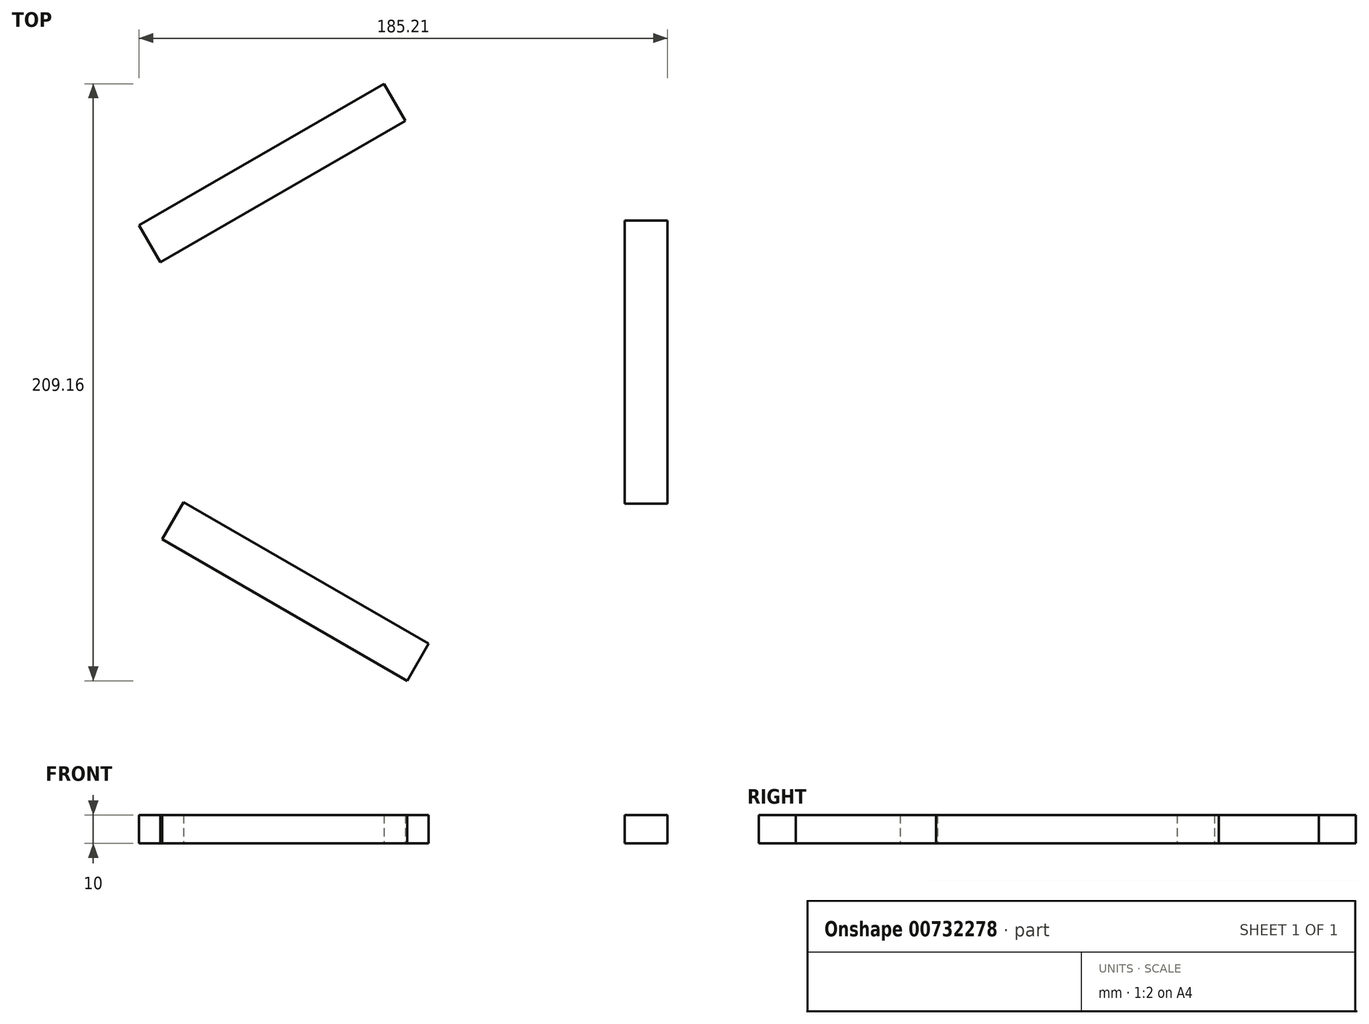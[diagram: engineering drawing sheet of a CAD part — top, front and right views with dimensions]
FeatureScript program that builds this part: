
annotation { "Feature Type Name" : "Feature", "Feature Type Description" : "" }
export const myFeature = defineFeature(function(context is Context, id is Id, definition is map)
    precondition{}
    {
        {
            var Q0;
            Q0=qCreatedBy(makeId("Top.planeOp"),FACE);
            var sketch = newSketch(context, id + "F0", { "sketchPlane" : qUnion([Q0])});
            skLineSegment(sketch, "E0.bottom", {"start": v(-44.37, 77.42) * mm, "end": v(-57.36, 84.92) * mm});
            skLineSegment(sketch, "E0.top", {"start": v(-93.94, -8.43) * mm, "end": v(-106.93, -0.93) * mm});
            skLineSegment(sketch, "E0.left", {"start": v(-44.37, 77.42) * mm, "end": v(-93.94, -8.43) * mm});
            skLineSegment(sketch, "E0.right", {"start": v(-57.36, 84.92) * mm, "end": v(-106.93, -0.93) * mm});
            skPoint(sketch, "E0.middle", {"position": v(-78.55, -220.5) * mm});
            skCircle(sketch, "E1", {"center": v(0, 0) * mm, "radius": 77.14 * mm, "construction": true});
            skLineSegment(sketch, "E2", {"start": v(-75.65, 38.25) * mm, "end": v(-53.37, 76.84) * mm});
            skLineSegment(sketch, "E3", {"start": v(-75.65, 38.25) * mm, "end": v(-97.94, -0.35) * mm});
            skLineSegment(sketch, "E4.bottom", {"start": v(51.27, 95.48) * mm, "end": v(38.28, 87.98) * mm});
            skLineSegment(sketch, "E4.top", {"start": v(100.84, 9.62) * mm, "end": v(87.85, 2.12) * mm});
            skLineSegment(sketch, "E4.left", {"start": v(51.27, 95.48) * mm, "end": v(100.84, 9.62) * mm});
            skLineSegment(sketch, "E4.right", {"start": v(38.28, 87.98) * mm, "end": v(87.85, 2.12) * mm});
            skPoint(sketch, "E4.middle", {"position": v(69.56, 48.8) * mm});
            skLineSegment(sketch, "E5", {"start": v(69.56, 48.8) * mm, "end": v(47.28, 87.4) * mm});
            skLineSegment(sketch, "E6", {"start": v(69.56, 48.8) * mm, "end": v(91.85, 10.2) * mm});
            skLineSegment(sketch, "E7.bottom", {"start": v(-48.28, -78.45) * mm, "end": v(-48.28, -93.45) * mm});
            skLineSegment(sketch, "E7.top", {"start": v(50.86, -78.45) * mm, "end": v(50.86, -93.45) * mm});
            skLineSegment(sketch, "E7.left", {"start": v(-48.28, -78.45) * mm, "end": v(50.86, -78.45) * mm});
            skLineSegment(sketch, "E7.right", {"start": v(-48.28, -93.45) * mm, "end": v(50.86, -93.45) * mm});
            skPoint(sketch, "E7.middle", {"position": v(1.3, -85.95) * mm});
            skLineSegment(sketch, "E8", {"start": v(1.3, -85.95) * mm, "end": v(-43.28, -85.95) * mm});
            skLineSegment(sketch, "E9", {"start": v(1.3, -85.95) * mm, "end": v(45.86, -85.95) * mm});
            skLineSegment(sketch, "E10.bottom", {"start": v(-9.28, 107.28) * mm, "end": v(-22.27, 114.78) * mm});
            skLineSegment(sketch, "E10.top", {"start": v(-108.84, -65.17) * mm, "end": v(-121.83, -57.67) * mm});
            skLineSegment(sketch, "E10.left", {"start": v(-9.28, 107.28) * mm, "end": v(-108.84, -65.17) * mm});
            skLineSegment(sketch, "E10.right", {"start": v(-22.27, 114.78) * mm, "end": v(-121.83, -57.67) * mm});
            skSolve(sketch);
        }
        {
            var Q0;
            Q0=makeQuery(id+"F0.imprint","IMPRINT",FACE,{"disambiguationData":[TD([[makeQuery(id+"F0.imprint","IMPRINT",EDGE,{"derivedFrom":sQuery(id+"F0.wireOp",EDGE,"E0.bottom")}),1.0]])]});
            extrude(context, id + "F1", {"entities" : qUnion([Q0]), "depth" : 10 * mm, "offsetDistance" : 25 * mm});
        }
        {
            var Q0;
            Q0=makeQuery(id+"F1.opExtrude","SWEPT_BODY",BODY,{"disambiguationData":[OSD([sQuery(id+"F0.wireOp",EDGE,"E0.bottom"),sQuery(id+"F0.wireOp",EDGE,"E0.top"),sQuery(id+"F0.wireOp",EDGE,"E0.left"),sQuery(id+"F0.wireOp",EDGE,"E0.right")])]});
            var Q1;
            Q1=sQuery(id+"F0.wireOp",EDGE,"E1");
            transform(context, id + "F2", {"entities" : qUnion([Q0]), "transformType" : TransformType.ROTATION, "transformAxis" : qUnion([Q1]), "angle" : 30 * degree, "oppositeDirection" : true, "makeCopy" : false});
        }
        {
            var Q0;
            Q0=makeQuery(id+"F1.opExtrude","SWEPT_BODY",BODY,{"disambiguationData":[OSD([sQuery(id+"F0.wireOp",EDGE,"E0.bottom"),sQuery(id+"F0.wireOp",EDGE,"E0.top"),sQuery(id+"F0.wireOp",EDGE,"E0.left"),sQuery(id+"F0.wireOp",EDGE,"E0.right")])]});
            var Q1;
            Q1=sQuery(id+"F0.wireOp",EDGE,"E1");
            transform(context, id + "F3", {"entities" : qUnion([Q0]), "transformType" : TransformType.ROTATION, "transformAxis" : qUnion([Q1]), "angle" : 120 * degree, "oppositeDirection" : true, "makeCopy" : true});
        }
        {
            var Q0;
            Q0=makeQuery(id+"F3.opPattern","COPY",BODY,{"derivedFrom":makeQuery(id+"F1.opExtrude","SWEPT_BODY",BODY,{"disambiguationData":[OSD([sQuery(id+"F0.wireOp",EDGE,"E0.bottom"),sQuery(id+"F0.wireOp",EDGE,"E0.top"),sQuery(id+"F0.wireOp",EDGE,"E0.left"),sQuery(id+"F0.wireOp",EDGE,"E0.right")])]}),"instanceName":"1"});
            var Q1;
            Q1=sQuery(id+"F0.wireOp",EDGE,"E1");
            transform(context, id + "F4", {"entities" : qUnion([Q0]), "transformType" : TransformType.ROTATION, "transformAxis" : qUnion([Q1]), "angle" : 120 * degree, "oppositeDirection" : true, "makeCopy" : true});
        }
    });
